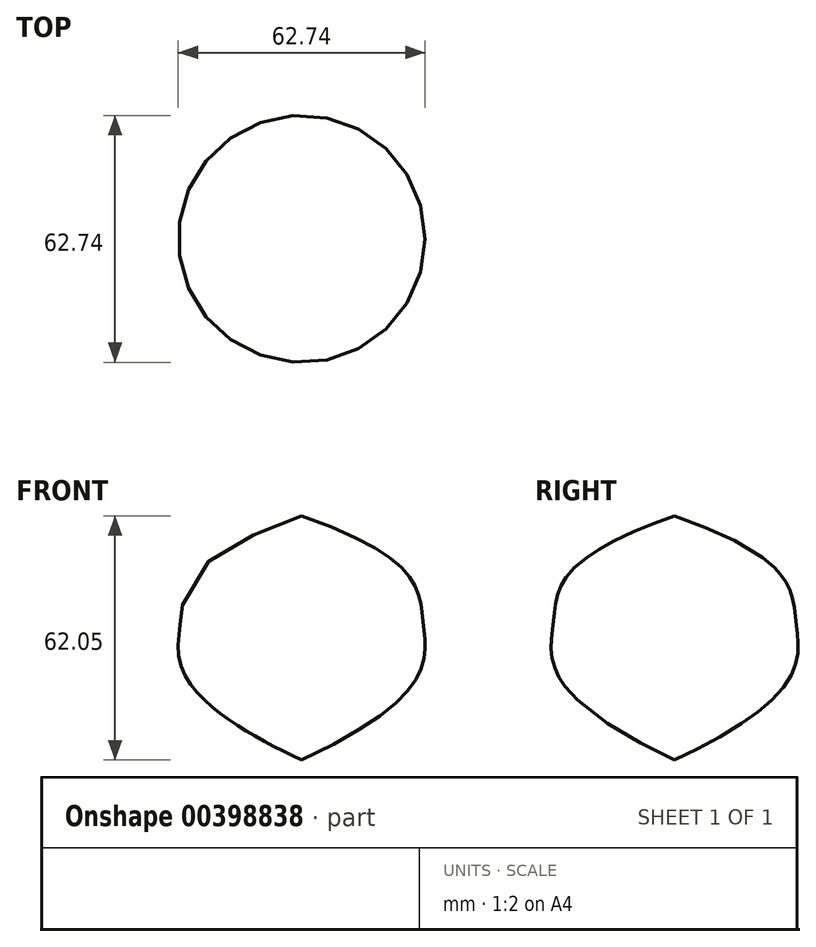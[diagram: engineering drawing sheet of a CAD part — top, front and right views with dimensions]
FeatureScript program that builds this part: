
annotation { "Feature Type Name" : "Feature", "Feature Type Description" : "" }
export const myFeature = defineFeature(function(context is Context, id is Id, definition is map)
    precondition{}
    {
        {
            var Q0;
            Q0=qCreatedBy(makeId("Front.planeOp"),FACE);
            var sketch = newSketch(context, id + "F0", { "sketchPlane" : qUnion([Q0])});
            skLineSegment(sketch, "E0", {"start": v(0, 27.14) * mm, "end": v(0, -34.9) * mm});
            skFitSpline(sketch, "E1", {"points": [v(0, 27.14) * mm, v(30.83, 0) * mm, v(0, -34.9) * mm], "startDerivative": vector(191.2, -67.1) * mm, "endDerivative": vector(-203.47, -95.95) * mm});
            skSolve(sketch);
        }
        {
            var Q0;
            Q0 = qSketchRegion(id + "F0", true);
            var Q1;
            Q1=sQuery(id+"F0.wireOp",EDGE,"E0");
            revolve(context, id + "F1", {"entities" : qUnion([Q0]), "axis" : qUnion([Q1]), "revolveType" : RevolveType.FULL});
        }
    });
